# Revit family: led_e_c_module_16w_4000k_clio_ct_ii_140066576
name_source: partatom
category: Leuchten
revit_build: Autodesk Revit 2016 (Build: 20190508_0715(x64)
units: mm (PartAtom-declared; Revit-internal decimal feet)

## family parameters
Basisbauteil = Fläche
Beim Laden mit Abzugskörper schneiden = Nein
Bemaßung runder Anschluss = Durchmesser verwenden
Gemeinsam genutzt = Nein
Lichtquelle = Nein
Raumberechnungspunkt = Nein
Teiletyp = Normal

## types (1)
- LED E C module 16W 4000K Clio CT II (1 x LED, 1800 lm)
    Approval mark = CE
    Beschreibung = Fits well in slim ceiling luminaires. Easy and flexible installation. Shadow free, homogeneous light diffusion. Integrated driver. Including magnets and connection box. Daylight and motion sensor accessory available.
    CIE Flux Codes = 29 63 90 95 100
    Height = 29 mm
    Hersteller = OPPLE
    Lamp Light Flux = 1800 lm
    Lamp count = 1
    Lampe = 1 x LED
    Length = 191 mm
    Luminous efficacy = 113 lm/W
    ModVariant = Nein
    Modell = 140066576
    Mounting Place = Ceiling, Wall
    Mounting Type = Surface mounted
    Number of Poles = 1
    OnlyDefault = Ja
    Power Factor = 1
    Product Name = LED E C module 16W 4000K Clio CT II
    Product group = Module Clio G2
    ProductGroupID = 315
    Protection Class = Protection class I
    Protection Degree = IP 20
    RLX_Detail_Level = 1
    RlxData = <blob elided: 21189 chars, md5=d85bcfbb>
    Scheinlast = 16 VA
    Socket = socket
    Standby Power = 0 W
    System Light Flux = 1807 lm
    System Power = 16 W
    Typenbild = 140066576.jpg
    Typenkommentare = Product without accessories
    URL = http://relux.com
    VarID = ---
    Voltage = 0 V
    Vorgabe-Ansicht = 1800 mm  [stored 5.90551 ft]
    Weight = 0.00 kg
    Width = 0 mm  [stored 0 ft]

note: [stored X ft] marks values corroborated as IEEE doubles in the binary element streams (Revit-internal decimal feet)

## geometry (parser evidence)
native form markers: Blend x4, Sweep x13
no freeform markers — native parametric forms only
